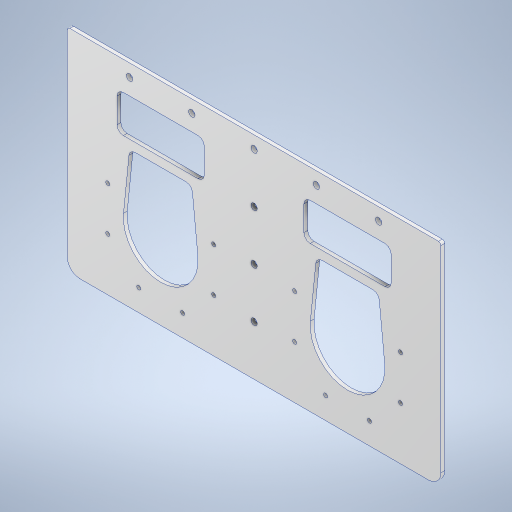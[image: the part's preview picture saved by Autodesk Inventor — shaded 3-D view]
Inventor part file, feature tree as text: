
AUTODESK INVENTOR PART (.ipt)
format: ipt  version: 2024.3 (Build 283343000, 343)  size: 448,000 bytes
history: native  units: mm
features: sketch x7, extrude x5, fillet x3, hole x2, other x1
ambient origin geometry x8: Origin, YZ Plane, XZ Plane, XY Plane, X Axis, Y Axis, Z Axis, Center Point
bodies: Body1 (feature_tree)
feature tree (18):
  other  "ソリッド1"
  extrude  "押し出し1"  Depth=175.0mm
  extrude  "押し出し2"  Depth=300.0mm
  extrude  "押し出し3"  Depth=3.0mm TaperAngle=0.0deg
  extrude  "押し出し4"  TaperAngle=0.0deg  [1 undecoded]
  fillet  "フィレット2"  [1 undecoded]
  extrude  "押し出し5"  Depth=150.0mm
  fillet  "フィレット6"  Radius=75.0mm
  fillet  "フィレット7"  Radius=5.0mm
  hole  "穴3"  [1 undecoded]
  hole  "穴4"  [1 undecoded]
  sketch  "スケッチ1"
  sketch  "スケッチ2"
  sketch  "スケッチ3"
  sketch  "スケッチ4"
  sketch  "スケッチ5"
  sketch  "スケッチ12"
  sketch  "スケッチ14"
note: 4 required parameter values undecoded (feature->parameter linkage not recoverable at this tier; creation-order binding heuristic only, values carry confidence <= 0.55)
